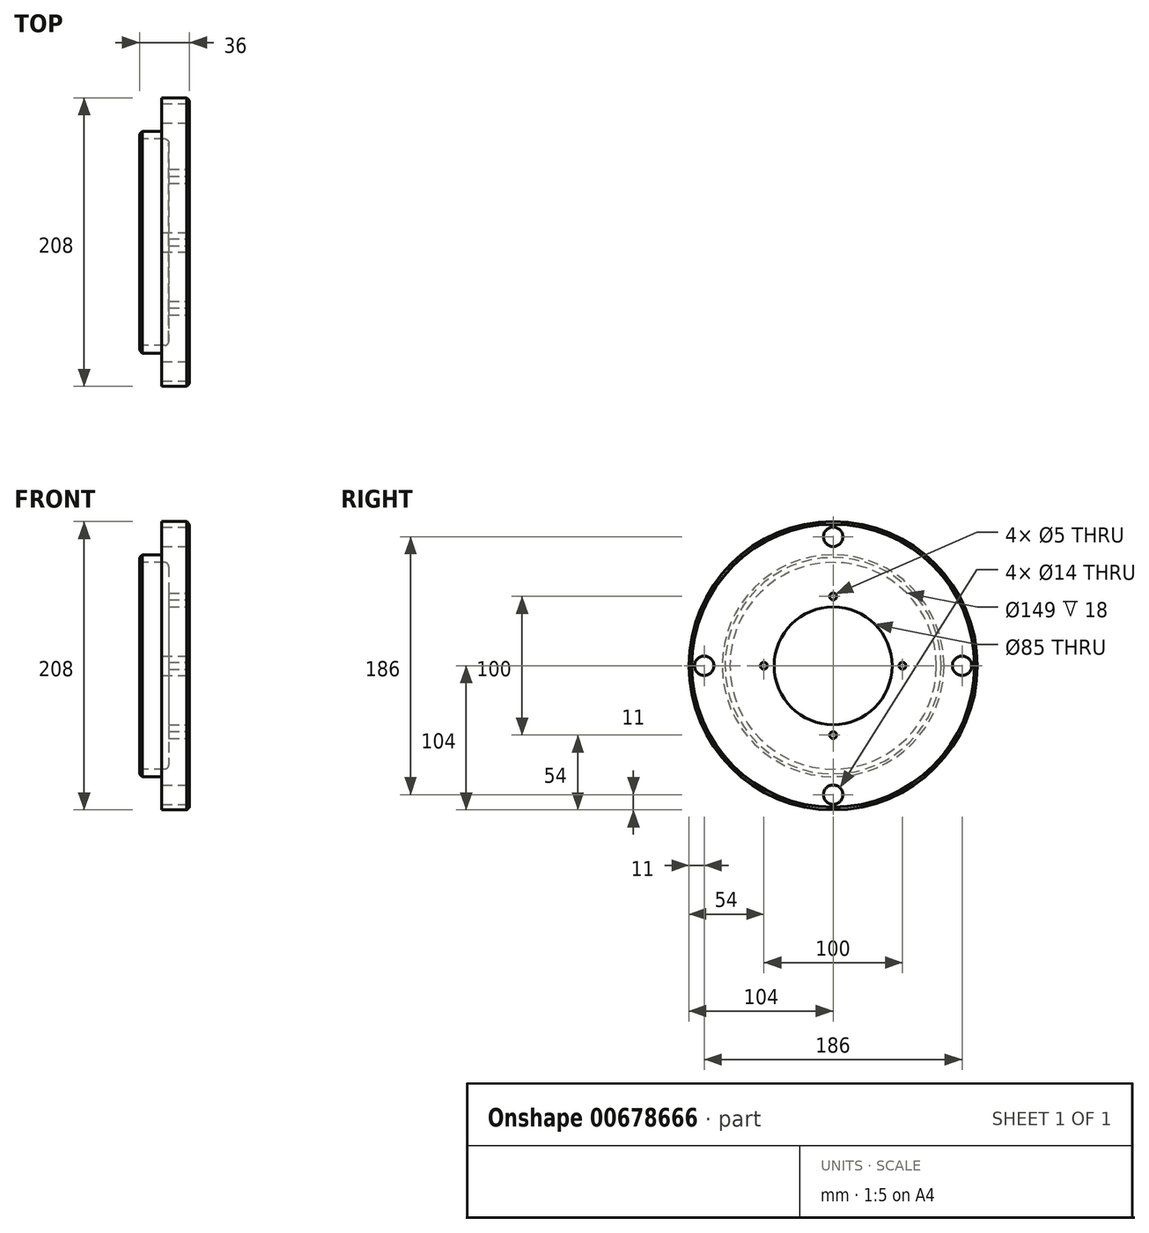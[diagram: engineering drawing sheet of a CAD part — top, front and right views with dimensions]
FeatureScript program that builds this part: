
annotation { "Feature Type Name" : "Feature", "Feature Type Description" : "" }
export const myFeature = defineFeature(function(context is Context, id is Id, definition is map)
    precondition{}
    {
        {
            var Q0;
            Q0=qCreatedBy(makeId("Right.planeOp"),FACE);
            var sketch = newSketch(context, id + "F0", { "sketchPlane" : qUnion([Q0])});
            skCircle(sketch, "E0", {"center": v(0, 0) * mm, "radius": 104 * mm});
            skSolve(sketch);
        }
        {
            var Q0;
            Q0 = qSketchRegion(id + "F0", true);
            extrude(context, id + "F1", {"entities" : qUnion([Q0]), "depth" : 20 * mm, "offsetDistance" : 25 * mm});
        }
        {
            var Q0;
            Q0=makeQuery(id+"F1.opExtrude","CAP_FACE",FACE,{"disambiguationData":[OSD([sQuery(id+"F0.wireOp",EDGE,"E0")])],"isStart":true});
            var sketch = newSketch(context, id + "F2", { "sketchPlane" : qUnion([Q0])});
            skCircle(sketch, "E1", {"center": v(0, 0) * mm, "radius": 80 * mm});
            skSolve(sketch);
        }
        {
            var Q0;
            Q0 = qSketchRegion(id + "F2", true);
            extrude(context, id + "F3", {"entities" : qUnion([Q0]), "operationType" : NewBodyOperationType.ADD, "depth" : 16 * mm, "offsetDistance" : 25 * mm});
        }
        {
            var Q0;
            Q0=makeQuery(id+"F3.opExtrude","CAP_EDGE",EDGE,{"disambiguationData":[OSD([sQuery(id+"F2.wireOp",EDGE,"E1")])],"isStart":false});
            var Q1;
            Q1=makeQuery(id+"F1.opExtrude","CAP_EDGE",EDGE,{"disambiguationData":[OSD([sQuery(id+"F0.wireOp",EDGE,"E0")])],"isStart":false});
            chamfer(context, id + "F4", {"entities" : qUnion([Q0, Q1]), "width" : 2 * mm, "tangentPropagation" : true});
        }
        {
            var Q0;
            Q0=makeQuery(id+"F3.opExtrude","CAP_FACE",FACE,{"disambiguationData":[OSD([sQuery(id+"F2.wireOp",EDGE,"E1")])],"isStart":false});
            var sketch = newSketch(context, id + "F5", { "sketchPlane" : qUnion([Q0])});
            skCircle(sketch, "E2", {"center": v(0, 0) * mm, "radius": 74.5 * mm});
            skSolve(sketch);
        }
        {
            var Q0;
            Q0 = qSketchRegion(id + "F5", true);
            extrude(context, id + "F6", {"entities" : qUnion([Q0]), "operationType" : NewBodyOperationType.REMOVE, "oppositeDirection" : true, "depth" : 21 * mm, "offsetDistance" : 25 * mm});
        }
        {
            var Q0;
            Q0=makeQuery(id+"F6.boolean.opBoolean","COPY",EDGE,{"derivedFrom":makeQuery(id+"F6.opExtrude","CAP_EDGE",EDGE,{"disambiguationData":[OSD([sQuery(id+"F5.wireOp",EDGE,"E2")])],"isStart":false})});
            fillet(context, id + "F7", {"entities" : qUnion([Q0]), "radius" : 3 * mm, "tangentPropagation" : true, "allowEdgeOverflow" : false});
        }
        {
            var Q0;
            Q0=makeQuery(id+"F1.opExtrude","CAP_FACE",FACE,{"disambiguationData":[OSD([sQuery(id+"F0.wireOp",EDGE,"E0")])],"isStart":false});
            var sketch = newSketch(context, id + "F8", { "sketchPlane" : qUnion([Q0])});
            skPoint(sketch, "E3", {"position": v(0, 0) * mm});
            skSolve(sketch);
        }
        {
            var Q0;
            Q0=sQuery(id+"F8.wireOp",VERTEX,"E3");
            var Q1;
            Q1=makeQuery(id+"F1.opExtrude","SWEPT_BODY",BODY,{"disambiguationData":[OSD([sQuery(id+"F0.wireOp",EDGE,"E0")])]});
            hole(context, id + "F9", {"style" : HoleStyle.SIMPLE, "endStyle" : HoleEndStyle.THROUGH, "holeDiameter" : 85 * mm, "majorDiameter" : 5 * mm, "isTappedThrough" : true, "tappedDepth" : 24.75 * mm, "tapClearance" : 3, "locations" : qUnion([Q0]), "scope" : qUnion([Q1])});
        }
        {
            var Q0;
            Q0=makeQuery(id+"F1.opExtrude","CAP_FACE",FACE,{"disambiguationData":[OSD([sQuery(id+"F0.wireOp",EDGE,"E0")])],"isStart":false});
            var sketch = newSketch(context, id + "F10", { "sketchPlane" : qUnion([Q0])});
            skCircle(sketch, "E4", {"center": v(0, 0) * mm, "radius": 50 * mm, "construction": true});
            skLineSegment(sketch, "E5", {"start": v(0, 0) * mm, "end": v(0, 50) * mm, "construction": true});
            skPoint(sketch, "E6", {"position": v(0, 50) * mm});
            skPoint(sketch, "E7.1.0", {"position": v(-50, 0) * mm});
            skPoint(sketch, "E7.2.0", {"position": v(0, -50) * mm});
            skPoint(sketch, "E7.3.0", {"position": v(50, 0) * mm});
            skSolve(sketch);
        }
        {
            var Q0;
            Q0=sQuery(id+"F10.wireOp",VERTEX,"E6");
            var Q1;
            Q1=sQuery(id+"F10.wireOp",VERTEX,"E7.3.0");
            var Q2;
            Q2=sQuery(id+"F10.wireOp",VERTEX,"E7.2.0");
            var Q3;
            Q3=sQuery(id+"F10.wireOp",VERTEX,"E7.1.0");
            var Q4;
            Q4=makeQuery(id+"F1.opExtrude","SWEPT_BODY",BODY,{"disambiguationData":[OSD([sQuery(id+"F0.wireOp",EDGE,"E0")])]});
            hole(context, id + "F11", {"style" : HoleStyle.SIMPLE, "endStyle" : HoleEndStyle.THROUGH, "standardTappedOrClearance" : lookupTablePath({ "standard" : "ISO", "engagement" : "75%", "pitch" : "1 mm", "size" : "M6", "type" : "Tapped" }), "standardBlindInLast" : lookupTablePath({ "standard" : "ISO", "engagement" : "75%", "pitch" : "1 mm", "size" : "M6", "type" : "Tapped" }), "holeDiameter" : 5 * mm, "majorDiameter" : 6 * mm, "showTappedDepth" : true, "isTappedThrough" : true, "tappedDepth" : 24.75 * mm, "tapClearance" : 3, "locations" : qUnion([Q0, Q1, Q2, Q3]), "scope" : qUnion([Q4])});
        }
        {
            var Q0;
            Q0=makeQuery(id+"F1.opExtrude","CAP_FACE",FACE,{"disambiguationData":[OSD([sQuery(id+"F0.wireOp",EDGE,"E0")])],"isStart":false});
            var sketch = newSketch(context, id + "F12", { "sketchPlane" : qUnion([Q0])});
            skCircle(sketch, "E8", {"center": v(0, 0) * mm, "radius": 93 * mm, "construction": true});
            skLineSegment(sketch, "E9", {"start": v(0, 0) * mm, "end": v(0, 131.06) * mm, "construction": true});
            skPoint(sketch, "E10", {"position": v(0, 93) * mm});
            skPoint(sketch, "E11.1.0", {"position": v(-93, 0) * mm});
            skPoint(sketch, "E11.2.0", {"position": v(0, -93) * mm});
            skPoint(sketch, "E11.3.0", {"position": v(93, 0) * mm});
            skSolve(sketch);
        }
        {
            var Q0;
            Q0=sQuery(id+"F12.wireOp",VERTEX,"E10");
            var Q1;
            Q1=sQuery(id+"F12.wireOp",VERTEX,"E11.3.0");
            var Q2;
            Q2=sQuery(id+"F12.wireOp",VERTEX,"E11.2.0");
            var Q3;
            Q3=sQuery(id+"F12.wireOp",VERTEX,"E11.1.0");
            var Q4;
            Q4=makeQuery(id+"F1.opExtrude","SWEPT_BODY",BODY,{"disambiguationData":[OSD([sQuery(id+"F0.wireOp",EDGE,"E0")])]});
            hole(context, id + "F13", {"style" : HoleStyle.SIMPLE, "endStyle" : HoleEndStyle.THROUGH, "holeDiameter" : 14 * mm, "majorDiameter" : 6 * mm, "isTappedThrough" : true, "tappedDepth" : 24.75 * mm, "tapClearance" : 3, "locations" : qUnion([Q0, Q1, Q2, Q3]), "scope" : qUnion([Q4])});
        }
    });
